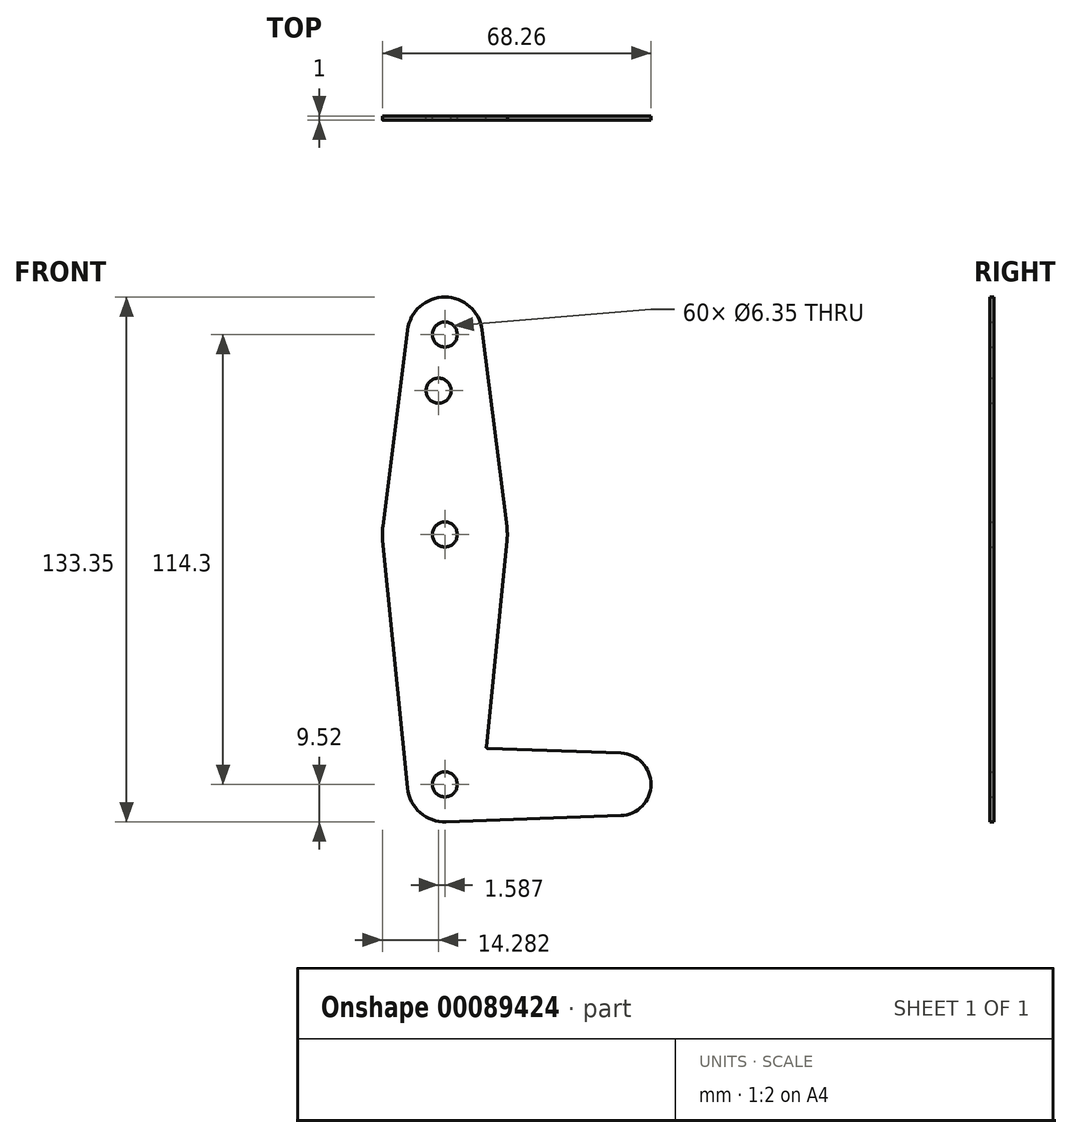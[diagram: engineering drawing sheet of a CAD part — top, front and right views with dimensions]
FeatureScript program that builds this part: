
annotation { "Feature Type Name" : "Feature", "Feature Type Description" : "" }
export const myFeature = defineFeature(function(context is Context, id is Id, definition is map)
    precondition{}
    {
        {
            var Q0;
            Q0=qCreatedBy(makeId("Front.planeOp"),FACE);
            var sketch = newSketch(context, id + "F0", { "sketchPlane" : qUnion([Q0])});
            skLineSegment(sketch, "E0", {"start": v(0, 114.3) * mm, "end": v(0, 0) * mm, "construction": true});
            skLineSegment(sketch, "E1", {"start": v(0, 0) * mm, "end": v(44.45, 0) * mm, "construction": true});
            skCircle(sketch, "E2", {"center": v(0, 114.3) * mm, "radius": 9.53 * mm});
            skCircle(sketch, "E3", {"center": v(0, 0) * mm, "radius": 9.53 * mm});
            skCircle(sketch, "E4", {"center": v(44.45, 0) * mm, "radius": 7.94 * mm});
            skCircle(sketch, "E5", {"center": v(0, 114.3) * mm, "radius": 3.18 * mm});
            skCircle(sketch, "E6", {"center": v(0, 0) * mm, "radius": 3.18 * mm});
            skCircle(sketch, "E7", {"center": v(0, 63.5) * mm, "radius": 15.88 * mm});
            skCircle(sketch, "E8", {"center": v(0, 63.5) * mm, "radius": 3.18 * mm});
            skLineSegment(sketch, "E9", {"start": v(-9.45, 115.5) * mm, "end": v(-15.75, 65.48) * mm});
            skLineSegment(sketch, "E10", {"start": v(-15.8, 61.91) * mm, "end": v(-9.48, -0.95) * mm});
            skLineSegment(sketch, "E11", {"start": v(9.45, 115.5) * mm, "end": v(15.75, 65.48) * mm});
            skLineSegment(sketch, "E12", {"start": v(0.34, -9.52) * mm, "end": v(44.73, -7.93) * mm});
            skLineSegment(sketch, "E13", {"start": v(10.83, 9.14) * mm, "end": v(44.73, 7.93) * mm});
            skLineSegment(sketch, "E14", {"start": v(10.53, 9.49) * mm, "end": v(15.8, 61.91) * mm});
            skCircle(sketch, "E15", {"center": v(-1.59, 100.03) * mm, "radius": 3.18 * mm});
            skArc(sketch, "E16.filletArc", {"start": v(10.53, 9.49) * mm, "mid": v(10.6, 9.25) * mm, "end": v(10.83, 9.14) * mm});
            skSolve(sketch);
        }
        {
            var Q0;
            Q0 = qSketchRegion(id + "F0", true);
            extrude(context, id + "F1", {"entities" : qUnion([Q0]), "depth" : 1 * mm});
        }
    });
